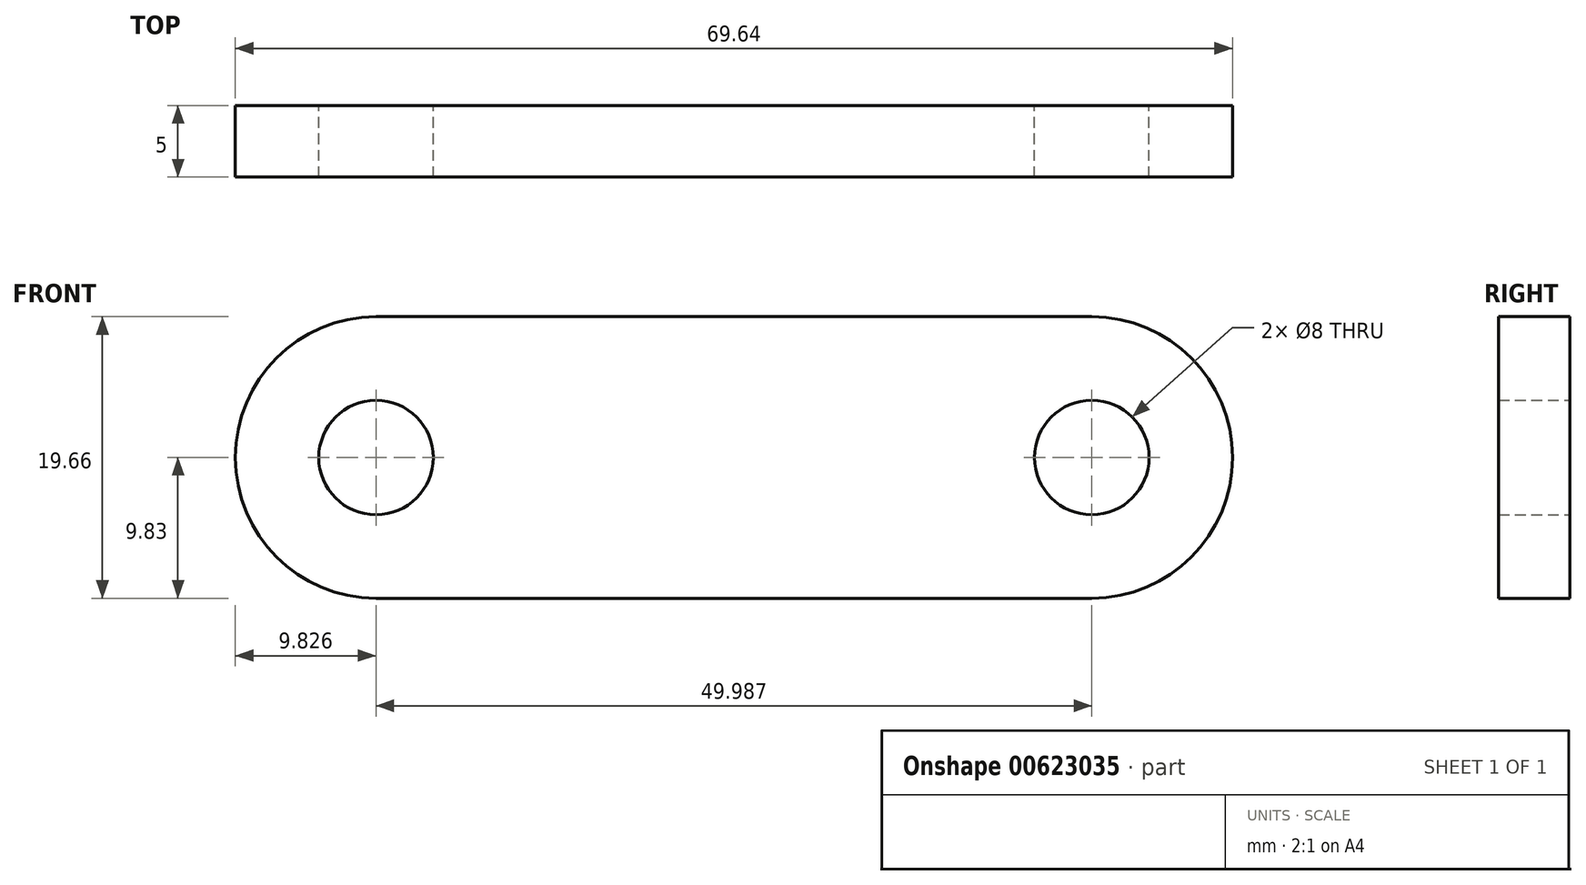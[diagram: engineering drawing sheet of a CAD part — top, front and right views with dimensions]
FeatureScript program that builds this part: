
annotation { "Feature Type Name" : "Feature", "Feature Type Description" : "" }
export const myFeature = defineFeature(function(context is Context, id is Id, definition is map)
    precondition{}
    {
        {
            var Q0;
            Q0=qCreatedBy(makeId("Front.planeOp"),FACE);
            var sketch = newSketch(context, id + "F0", { "sketchPlane" : qUnion([Q0])});
            skLineSegment(sketch, "E0", {"start": v(0, 0) * mm, "end": v(-25, 0) * mm});
            skLineSegment(sketch, "E1", {"start": v(0, 0) * mm, "end": v(0, 18.46) * mm});
            skArc(sketch, "E2", {"start": v(-25, 9.83) * mm, "mid": v(-34.82, 0) * mm, "end": v(-25, -9.83) * mm});
            skCircle(sketch, "E3", {"center": v(-25, 0) * mm, "radius": 4 * mm});
            skLineSegment(sketch, "E4.0", {"start": v(0, 9.83) * mm, "end": v(-25, 9.83) * mm});
            skLineSegment(sketch, "E5.0", {"start": v(0, -9.83) * mm, "end": v(-25, -9.83) * mm});
            skArc(sketch, "E6.MirrorCS", {"start": v(25, 9.83) * mm, "mid": v(34.82, 0) * mm, "end": v(25, -9.83) * mm});
            skCircle(sketch, "E7.MirrorC", {"center": v(25, 0) * mm, "radius": 4 * mm});
            skLineSegment(sketch, "E8.MirrorCS", {"start": v(0, 0) * mm, "end": v(25, 0) * mm});
            skLineSegment(sketch, "E9.MirrorCS", {"start": v(0, -9.83) * mm, "end": v(25, -9.83) * mm});
            skLineSegment(sketch, "E10.MirrorCS", {"start": v(0, 9.83) * mm, "end": v(25, 9.83) * mm});
            skSolve(sketch);
        }
        {
            var Q0;
            Q0=makeQuery(id+"F0.imprint","IMPRINT",FACE,{"disambiguationData":[TD([[makeQuery(id+"F0.imprint","IMPRINT",EDGE,{"derivedFrom":sQuery(id+"F0.wireOp",EDGE,"E2")}),1.0]])]});
            extrude(context, id + "F1", {"entities" : qUnion([Q0]), "endBound" : BoundingType.SYMMETRIC, "depth" : 5 * mm, "offsetDistance" : 25.4 * mm});
        }
    });
